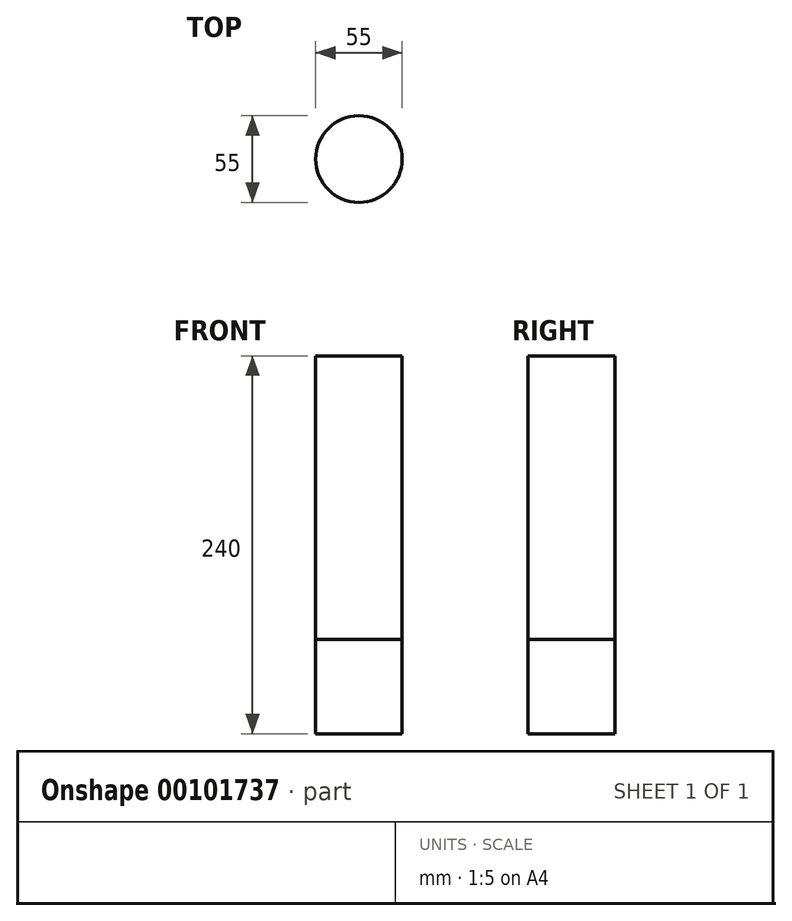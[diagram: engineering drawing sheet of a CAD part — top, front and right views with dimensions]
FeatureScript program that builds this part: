
annotation { "Feature Type Name" : "Feature", "Feature Type Description" : "" }
export const myFeature = defineFeature(function(context is Context, id is Id, definition is map)
    precondition{}
    {
        {
            var Q0;
            Q0=qCreatedBy(makeId("Top.planeOp"),FACE);
            var sketch = newSketch(context, id + "F0", { "sketchPlane" : qUnion([Q0])});
            skCircle(sketch, "E0", {"center": v(0, 0) * mm, "radius": 27.5 * mm});
            skSolve(sketch);
        }
        {
            var Q0;
            Q0=makeQuery(id+"F0.imprint","IMPRINT",FACE,{"disambiguationData":[TD([[makeQuery(id+"F0.imprint","IMPRINT",EDGE,{"derivedFrom":sQuery(id+"F0.wireOp",EDGE,"E0")}),1.0]])]});
            extrude(context, id + "F1", {"entities" : qUnion([Q0]), "oppositeDirection" : true, "depth" : 180 * mm});
        }
        {
            var Q0;
            Q0 = qSketchRegion(id + "F0", true);
            extrude(context, id + "F2", {"entities" : qUnion([Q0]), "oppositeDirection" : true, "depth" : 240 * mm});
        }
    });
